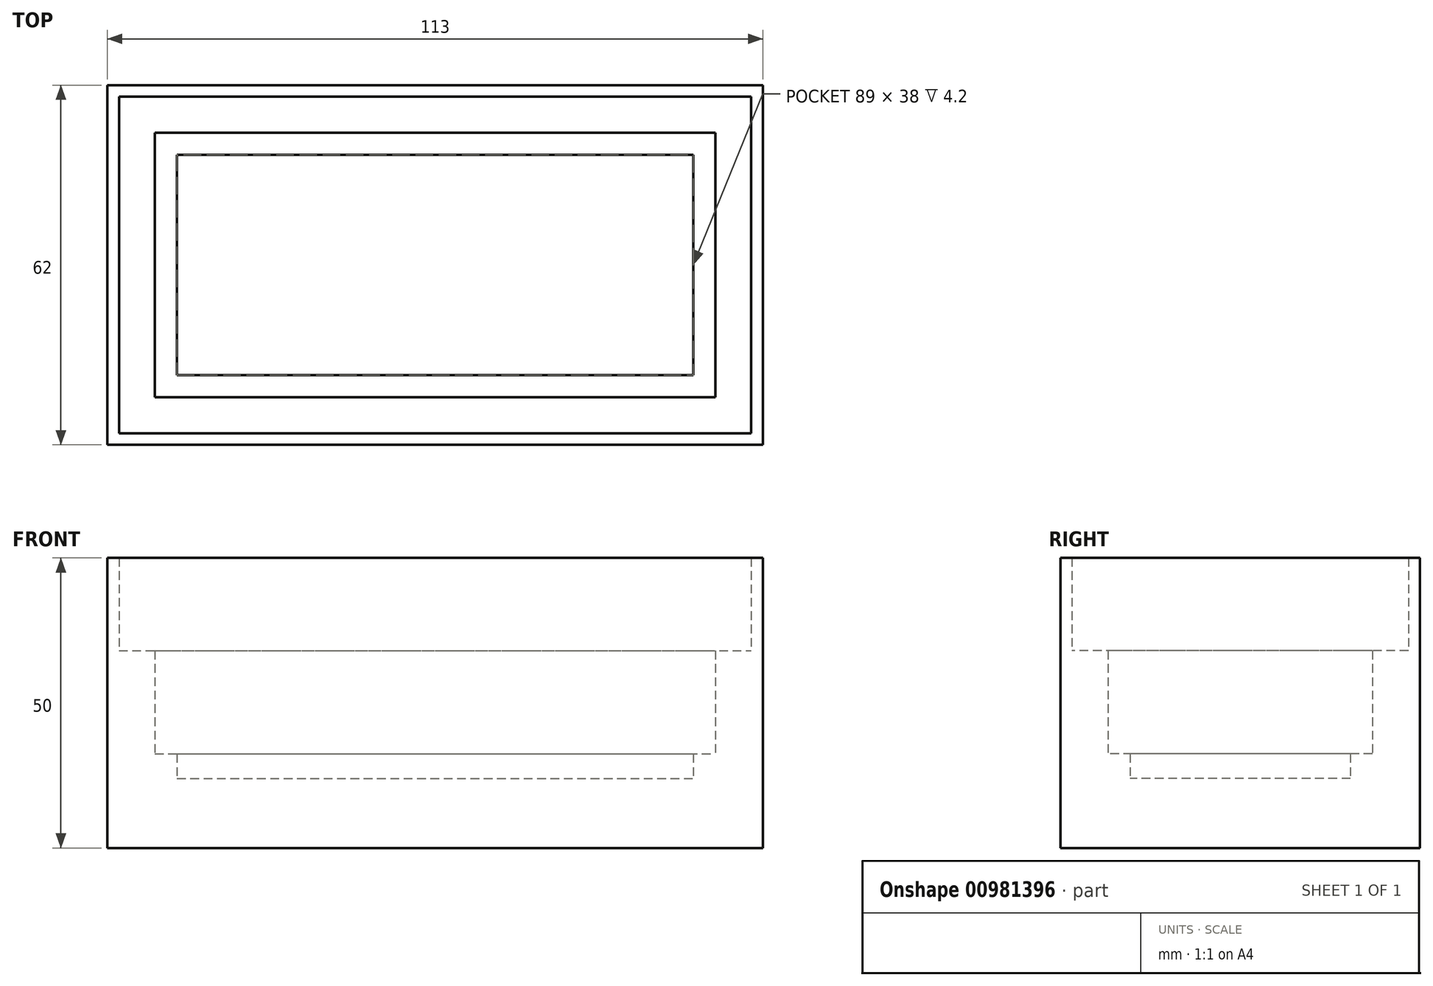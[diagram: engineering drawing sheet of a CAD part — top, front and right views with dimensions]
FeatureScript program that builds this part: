
annotation { "Feature Type Name" : "Feature", "Feature Type Description" : "" }
export const myFeature = defineFeature(function(context is Context, id is Id, definition is map)
    precondition{}
    {
        {
            var Q0;
            Q0=qCreatedBy(makeId("Top.planeOp"),FACE);
            var sketch = newSketch(context, id + "F0", { "sketchPlane" : qUnion([Q0])});
            skLineSegment(sketch, "E0.bottom", {"start": v(-59.5, 24.83) * mm, "end": v(53.5, 24.83) * mm});
            skLineSegment(sketch, "E0.top", {"start": v(-59.5, -37.17) * mm, "end": v(53.5, -37.17) * mm});
            skLineSegment(sketch, "E0.left", {"start": v(-59.5, 24.83) * mm, "end": v(-59.5, -37.17) * mm});
            skLineSegment(sketch, "E0.right", {"start": v(53.5, 24.83) * mm, "end": v(53.5, -37.17) * mm});
            skSolve(sketch);
        }
        {
            var Q0;
            Q0=makeQuery(id+"F0.imprint","IMPRINT",FACE,{"disambiguationData":[TD([[makeQuery(id+"F0.imprint","IMPRINT",EDGE,{"derivedFrom":sQuery(id+"F0.wireOp",EDGE,"E0.bottom")}),-1.0]])]});
            var Q1;
            Q1 = qSketchRegion(id + "F0", true);
            extrude(context, id + "F1", {"entities" : qUnion([Q0, Q1]), "depth" : 50 * mm, "offsetDistance" : 25.4 * mm});
        }
        {
            var Q0;
            Q0=makeQuery(id+"F1.opExtrude","CAP_FACE",FACE,{"disambiguationData":[OSD([sQuery(id+"F0.wireOp",EDGE,"E0.bottom"),sQuery(id+"F0.wireOp",EDGE,"E0.top"),sQuery(id+"F0.wireOp",EDGE,"E0.left"),sQuery(id+"F0.wireOp",EDGE,"E0.right")])],"isStart":false});
            shell(context, id + "F2", {"entities" : qUnion([Q0]), "thickness" : 2 * mm});
        }
        {
            var Q0;
            Q0=makeQuery(id+"F2.opShell","OFFSET_FACE",FACE,{"disambiguationData":[OSD([sQuery(id+"F0.wireOp",EDGE,"E0.bottom"),sQuery(id+"F0.wireOp",EDGE,"E0.top"),sQuery(id+"F0.wireOp",EDGE,"E0.left"),sQuery(id+"F0.wireOp",EDGE,"E0.right")])]});
            extrude(context, id + "F3", {"entities" : qUnion([Q0]), "operationType" : NewBodyOperationType.ADD, "depth" : 32 * mm, "offsetDistance" : 25.4 * mm});
        }
        {
            var Q0;
            Q0=makeQuery(id+"F3.opExtrude","CAP_FACE",FACE,{"disambiguationData":[OSD([sQuery(id+"F0.wireOp",EDGE,"E0.bottom"),sQuery(id+"F0.wireOp",EDGE,"E0.top"),sQuery(id+"F0.wireOp",EDGE,"E0.left"),sQuery(id+"F0.wireOp",EDGE,"E0.right")])],"isStart":false});
            shell(context, id + "F4", {"entities" : qUnion([Q0]), "thickness" : 8.2 * mm});
        }
        {
            var Q0;
            Q0=makeQuery(id+"F4.opShell","OFFSET_FACE",FACE,{"disambiguationData":[OSD([sQuery(id+"F0.wireOp",EDGE,"E0.bottom"),sQuery(id+"F0.wireOp",EDGE,"E0.top"),sQuery(id+"F0.wireOp",EDGE,"E0.left"),sQuery(id+"F0.wireOp",EDGE,"E0.right")])]});
            extrude(context, id + "F5", {"entities" : qUnion([Q0]), "operationType" : NewBodyOperationType.ADD, "depth" : 8 * mm, "offsetDistance" : 25.4 * mm});
        }
        {
            var Q0;
            Q0=makeQuery(id+"F5.opExtrude","CAP_FACE",FACE,{"disambiguationData":[OSD([sQuery(id+"F0.wireOp",EDGE,"E0.bottom"),sQuery(id+"F0.wireOp",EDGE,"E0.top"),sQuery(id+"F0.wireOp",EDGE,"E0.left"),sQuery(id+"F0.wireOp",EDGE,"E0.right")])],"isStart":false});
            shell(context, id + "F6", {"entities" : qUnion([Q0]), "thickness" : 12 * mm});
        }
    });
